# Revit family: Desk-Teknion-JNWDSE-Double_Sided_Rectangular_Exposed-R2018
name_source: partatom
category: Furniture
revit_build: Autodesk Revit 2018 (Build: 20190510_1515(x64)
units: mm (PartAtom-declared; Revit-internal decimal feet)

## family parameters
Always vertical = Yes
Cut with Voids When Loaded = No
OmniClass Number = 23.40.20.00
OmniClass Title = General Furniture and Specialties
Room Calculation Point = No
Shared = Yes
Work Plane-Based = No

## types (2) — shared parameters
Assembly Code = E2020200
Manufacturer = Teknion
Manufacturer Fax = 416.661.4586
Part Number = JNWDSE
Product Documentation Link = http://www.teknion.com
Product Line = Cityline
Product Page URL = http://www.teknion.com
Series = Cityline
Sustainability Data = http://www.teknion.com
URL = www.teknion.com
Unit Weight URL = http://www.teknion.com
Warranty = http://www.teknion.com

## per-type parameters (varying)
| type | Description | Model |
| Double-Sided Beam | Double-Sided Rectangular Worksurface - Exposed Beam, Double-Sided Beam | JNWDSED___ |
| Single-Sided Beam | Double-Sided Rectangular Worksurface - Exposed Beam, Single-Sided Beam | JNWDSES___ |

type visibility flags: 2 boolean params named "<type name>" — each type sets only its own to Yes (folded from table)

## geometry (parser evidence)
native form markers: Sweep x2
no freeform markers — native parametric forms only
